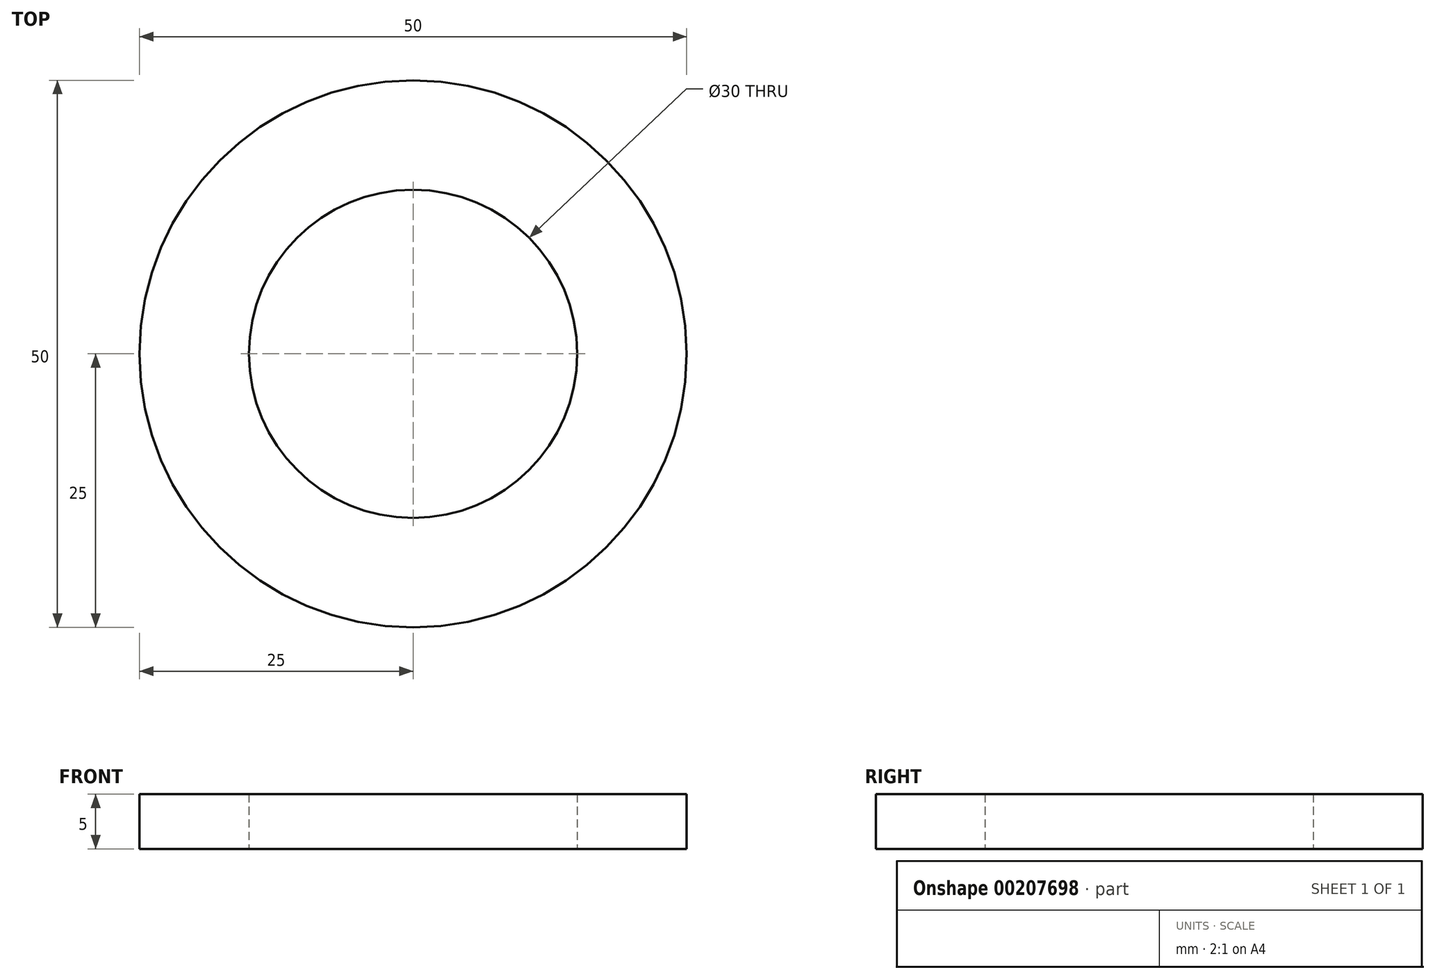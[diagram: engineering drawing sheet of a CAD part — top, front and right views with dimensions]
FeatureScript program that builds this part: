
annotation { "Feature Type Name" : "Feature", "Feature Type Description" : "" }
export const myFeature = defineFeature(function(context is Context, id is Id, definition is map)
    precondition{}
    {
        {
            var Q0;
            Q0=qCreatedBy(makeId("Top.planeOp"),FACE);
            var sketch = newSketch(context, id + "F0", { "sketchPlane" : qUnion([Q0])});
            skCircle(sketch, "E0", {"center": v(0, 0) * mm, "radius": 25 * mm});
            skCircle(sketch, "E1", {"center": v(0, 0) * mm, "radius": 15 * mm});
            skSolve(sketch);
        }
        {
            var Q0;
            Q0=makeQuery(id+"F0.imprint","IMPRINT",FACE,{"disambiguationData":[TD([[makeQuery(id+"F0.imprint","IMPRINT",EDGE,{"derivedFrom":sQuery(id+"F0.wireOp",EDGE,"E0")}),1.0]])]});
            extrude(context, id + "F1", {"entities" : qUnion([Q0]), "endBound" : BoundingType.SYMMETRIC, "depth" : 5 * mm});
        }
    });
